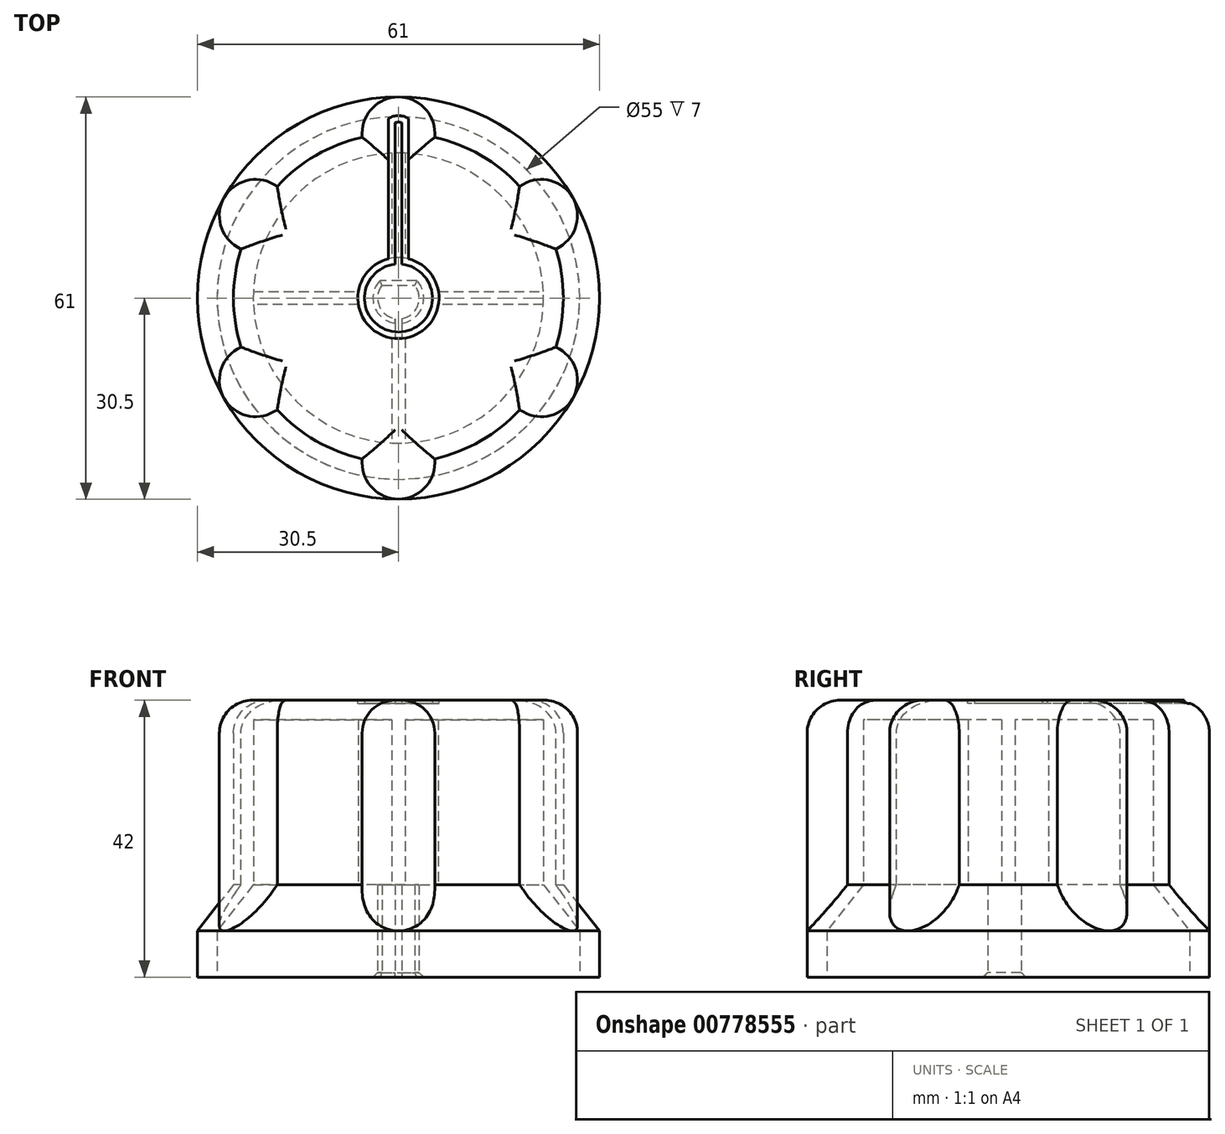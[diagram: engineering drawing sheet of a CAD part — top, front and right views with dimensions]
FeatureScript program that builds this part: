
annotation { "Feature Type Name" : "Feature", "Feature Type Description" : "" }
export const myFeature = defineFeature(function(context is Context, id is Id, definition is map)
    precondition{}
    {
        {
            var Q0;
            Q0=qCreatedBy(makeId("Top.planeOp"),FACE);
            var sketch = newSketch(context, id + "F0", { "sketchPlane" : qUnion([Q0])});
            skCircle(sketch, "E0", {"center": v(0, 0) * mm, "radius": 3.15 * mm});
            skLineSegment(sketch, "E1", {"start": v(-2.47, 1.95) * mm, "end": v(2.47, 1.95) * mm});
            skCircle(sketch, "E2", {"center": v(0, 0) * mm, "radius": 30.5 * mm});
            skCircle(sketch, "E3.0", {"center": v(0, 0) * mm, "radius": 6.15 * mm});
            skLineSegment(sketch, "E4", {"start": v(-0.5, -3.11) * mm, "end": v(-0.5, -6.13) * mm});
            skLineSegment(sketch, "E5", {"start": v(0.5, -3.11) * mm, "end": v(0.5, -6.13) * mm});
            skCircle(sketch, "E6.0", {"center": v(0, 0) * mm, "radius": 27.5 * mm});
            skSolve(sketch);
        }
        {
            var Q0;
            {var subQ0=sQuery(id+"F0.wireOp",EDGE,"E4");Q0=makeQuery(id+"F0.imprint","IMPRINT",FACE,{"disambiguationData":[TD([[makeQuery(id+"F0.imprint","IMPRINT",EDGE,{"derivedFrom":subQ0}),-1.0]])]});}
            var Q1;
            {var subQ0=sQuery(id+"F0.wireOp",EDGE,"E1");Q1=makeQuery(id+"F0.imprint","IMPRINT",FACE,{"disambiguationData":[TD([[makeQuery(id+"F0.imprint","IMPRINT",EDGE,{"derivedFrom":subQ0}),1.0]])]});}
            extrude(context, id + "F1", {"entities" : qUnion([Q0, Q1]), "depth" : 14 * mm, "offsetDistance" : 25 * mm});
        }
        {
            var Q0;
            Q0=makeQuery(id+"F0.imprint","IMPRINT",FACE,{"disambiguationData":[TD([[makeQuery(id+"F0.imprint","IMPRINT",EDGE,{"derivedFrom":sQuery(id+"F0.wireOp",EDGE,"E2")}),1.0]])]});
            extrude(context, id + "F2", {"entities" : qUnion([Q0]), "depth" : 7 * mm, "offsetDistance" : 25 * mm});
        }
        {
            var Q0;
            Q0=makeQuery(id+"F1.opExtrude","CAP_FACE",FACE,{"disambiguationData":[OSD([sQuery(id+"F0.wireOp",EDGE,"E0"),sQuery(id+"F0.wireOp",EDGE,"E1"),sQuery(id+"F0.wireOp",EDGE,"E3.0"),sQuery(id+"F0.wireOp",EDGE,"E4"),sQuery(id+"F0.wireOp",EDGE,"E5")])],"isStart":false});
            var sketch = newSketch(context, id + "F3", { "sketchPlane" : qUnion([Q0])});
            skArc(sketch, "E7.0", {"start": v(0.5, -6.13) * mm, "mid": v(0, 6.15) * mm, "end": v(-0.5, -6.13) * mm});
            skCircle(sketch, "E8", {"center": v(0, 0) * mm, "radius": 25 * mm});
            skCircle(sketch, "E9.0", {"center": v(0, 0) * mm, "radius": 22 * mm});
            skSolve(sketch);
        }
        {
            var Q0;
            Q0=makeQuery(id+"F2.opExtrude","CAP_FACE",FACE,{"disambiguationData":[OSD([sQuery(id+"F0.wireOp",EDGE,"E2"),sQuery(id+"F0.wireOp",EDGE,"E6.0")])],"isStart":false});
            var sketch = newSketch(context, id + "F4", { "sketchPlane" : qUnion([Q0])});
            skCircle(sketch, "E10.0", {"center": v(0, 0) * mm, "radius": 27.5 * mm});
            skCircle(sketch, "E11.0.0", {"center": v(0, 0) * mm, "radius": 30.5 * mm});
            skSolve(sketch);
        }
        {
            var Q0;
            Q0=makeQuery(id+"F3.imprint","IMPRINT",FACE,{"disambiguationData":[TD([[makeQuery(id+"F3.imprint","IMPRINT",EDGE,{"derivedFrom":sQuery(id+"F3.wireOp",EDGE,"E8")}),1.0]])]});
            extrude(context, id + "F5", {"entities" : qUnion([Q0]), "depth" : 25 * mm, "offsetDistance" : 25 * mm});
        }
        {
            var Q0;
            Q0=qCreatedBy(makeId("Right.planeOp"),FACE);
            var sketch = newSketch(context, id + "F6", { "sketchPlane" : qUnion([Q0])});
            skLineSegment(sketch, "E12", {"start": v(-25, 14) * mm, "end": v(-25, 39) * mm});
            skLineSegment(sketch, "E13", {"start": v(-22, 14) * mm, "end": v(-22, 39) * mm});
            skLineSegment(sketch, "E14", {"start": v(22, 39) * mm, "end": v(22, 14) * mm});
            skLineSegment(sketch, "E15", {"start": v(-30.5, 0) * mm, "end": v(-30.5, 7) * mm});
            skLineSegment(sketch, "E16", {"start": v(30.5, 7) * mm, "end": v(30.5, 0) * mm});
            skLineSegment(sketch, "E17.0.0", {"start": v(-27.5, 7) * mm, "end": v(27.5, 7) * mm});
            skLineSegment(sketch, "E18", {"start": v(-22, 14) * mm, "end": v(-27.5, 7) * mm});
            skLineSegment(sketch, "E19", {"start": v(-25, 14) * mm, "end": v(-30.5, 7) * mm});
            skLineSegment(sketch, "E20.0.0", {"start": v(-30.5, 7) * mm, "end": v(30.5, 7) * mm});
            skLineSegment(sketch, "E21.0.0", {"start": v(25, 14) * mm, "end": v(-25, 14) * mm});
            skLineSegment(sketch, "E22.0", {"start": v(-22, 14) * mm, "end": v(22, 14) * mm});
            skSolve(sketch);
        }
        {
            var Q0;
            Q0=qCreatedBy(makeId("Front.planeOp"),FACE);
            var sketch = newSketch(context, id + "F7", { "sketchPlane" : qUnion([Q0])});
            skLineSegment(sketch, "E23", {"start": v(0, 0) * mm, "end": v(0, 40) * mm});
            skSolve(sketch);
        }
        {
            var Q0;
            {var subQ0=sQuery(id+"F6.wireOp",EDGE,"E18");Q0=makeQuery(id+"F6.imprint","IMPRINT",FACE,{"disambiguationData":[TD([[makeQuery(id+"F6.imprint","IMPRINT",EDGE,{"derivedFrom":subQ0}),-1.0]])]});}
            var Q1;
            Q1=sQuery(id+"F7.wireOp",EDGE,"E23");
            revolve(context, id + "F8", {"surfaceOperationType" : NewSurfaceOperationType.NEW, "entities" : qUnion([Q0]), "axis" : qUnion([Q1]), "revolveType" : RevolveType.FULL});
        }
        {
            var Q0;
            Q0=makeQuery(id+"F1.opExtrude","CAP_FACE",FACE,{"disambiguationData":[OSD([sQuery(id+"F0.wireOp",EDGE,"E0"),sQuery(id+"F0.wireOp",EDGE,"E1"),sQuery(id+"F0.wireOp",EDGE,"E3.0"),sQuery(id+"F0.wireOp",EDGE,"E4"),sQuery(id+"F0.wireOp",EDGE,"E5")])],"isStart":false});
            var sketch = newSketch(context, id + "F9", { "sketchPlane" : qUnion([Q0])});
            skCircle(sketch, "E24", {"center": v(0, 0) * mm, "radius": 6.15 * mm});
            skArc(sketch, "E25.0", {"start": v(0.5, -6.13) * mm, "mid": v(0, 6.15) * mm, "end": v(-0.5, -6.13) * mm});
            skCircle(sketch, "E26.0", {"center": v(0, 0) * mm, "radius": 22 * mm});
            skLineSegment(sketch, "E27", {"start": v(-21.98, 1) * mm, "end": v(-6.07, 1) * mm});
            skLineSegment(sketch, "E28", {"start": v(21.98, -1) * mm, "end": v(6.07, -1) * mm});
            skLineSegment(sketch, "E29", {"start": v(-1, 21.98) * mm, "end": v(-1, 6.07) * mm});
            skLineSegment(sketch, "E30", {"start": v(1, 21.98) * mm, "end": v(1, 6.07) * mm});
            skLineSegment(sketch, "E31.trimOffspring", {"start": v(6.07, 1) * mm, "end": v(21.98, 1) * mm});
            skLineSegment(sketch, "E32.trimOffspring", {"start": v(-6.07, -1) * mm, "end": v(-21.98, -1) * mm});
            skLineSegment(sketch, "E33.trimOffspring", {"start": v(1, -6.07) * mm, "end": v(1, -21.98) * mm});
            skLineSegment(sketch, "E34.trimOffspring", {"start": v(-1, -6.07) * mm, "end": v(-1, -21.98) * mm});
            skSolve(sketch);
        }
        {
            var Q0;
            {var subQ0=sQuery(id+"F9.wireOp",EDGE,"E29");Q0=makeQuery(id+"F9.imprint","IMPRINT",FACE,{"disambiguationData":[TD([[makeQuery(id+"F9.imprint","IMPRINT",EDGE,{"derivedFrom":subQ0}),1.0]])]});}
            var Q1;
            {var subQ9=sQuery(id+"F0.wireOp",EDGE,"E1");Q1=makeQuery(id+"F9.imprint","IMPRINT",FACE,{"disambiguationData":[TD([[makeQuery(id+"F9.imprint","IMPRINT",EDGE,{"derivedFrom":makeQuery(id+"F1.opExtrude","CAP_EDGE",EDGE,{"disambiguationData":[OSD([subQ9])],"isStart":false})}),1.0]])]});}
            var Q2;
            {var subQ0=sQuery(id+"F9.wireOp",EDGE,"E28");Q2=makeQuery(id+"F9.imprint","IMPRINT",FACE,{"disambiguationData":[TD([[makeQuery(id+"F9.imprint","IMPRINT",EDGE,{"derivedFrom":subQ0}),-1.0]])]});}
            var Q3;
            {var subQ2=sQuery(id+"F9.wireOp",EDGE,"E33.trimOffspring");Q3=makeQuery(id+"F9.imprint","IMPRINT",FACE,{"disambiguationData":[TD([[makeQuery(id+"F9.imprint","IMPRINT",EDGE,{"derivedFrom":subQ2}),-1.0]])]});}
            var Q4;
            {var subQ0=sQuery(id+"F9.wireOp",EDGE,"E27");Q4=makeQuery(id+"F9.imprint","IMPRINT",FACE,{"disambiguationData":[TD([[makeQuery(id+"F9.imprint","IMPRINT",EDGE,{"derivedFrom":subQ0}),-1.0]])]});}
            var Q5;
            {var subQ0=sQuery(id+"F0.wireOp",EDGE,"E1");Q5=makeQuery(id+"F9.imprint","IMPRINT",FACE,{"disambiguationData":[TD([[makeQuery(id+"F9.imprint","IMPRINT",EDGE,{"derivedFrom":makeQuery(id+"F1.opExtrude","CAP_EDGE",EDGE,{"disambiguationData":[OSD([subQ0])],"isStart":false})}),-1.0]])]});}
            var Q6;
            Q6=makeQuery(id+"F5.opExtrude","CAP_FACE",FACE,{"disambiguationData":[OSD([sQuery(id+"F3.wireOp",EDGE,"E8"),sQuery(id+"F3.wireOp",EDGE,"E9.0")])],"isStart":false});
            extrude(context, id + "F10", {"entities" : qUnion([Q0, Q1, Q2, Q3, Q4, Q5]), "operationType" : NewBodyOperationType.ADD, "endBound" : BoundingType.UP_TO_SURFACE, "depth" : 25 * mm, "endBoundEntityFace" : qUnion([Q6]), "offsetDistance" : 25 * mm});
        }
        {
            var Q0;
            Q0=makeQuery(id+"F5.opExtrude","CAP_FACE",FACE,{"disambiguationData":[OSD([sQuery(id+"F3.wireOp",EDGE,"E8"),sQuery(id+"F3.wireOp",EDGE,"E9.0")])],"isStart":false});
            var sketch = newSketch(context, id + "F11", { "sketchPlane" : qUnion([Q0])});
            skCircle(sketch, "E35.0", {"center": v(0, 0) * mm, "radius": 25 * mm});
            skSolve(sketch);
        }
        {
            var Q0;
            Q0 = qSketchRegion(id + "F11", true);
            extrude(context, id + "F12", {"entities" : qUnion([Q0]), "depth" : 3 * mm, "offsetDistance" : 25 * mm});
        }
        {
            var Q0;
            Q0=makeQuery(id+"F12.opExtrude","CAP_FACE",FACE,{"disambiguationData":[OSD([sQuery(id+"F11.wireOp",EDGE,"E35.0")])],"isStart":false});
            var sketch = newSketch(context, id + "F13", { "sketchPlane" : qUnion([Q0])});
            skCircle(sketch, "E36.0", {"center": v(0, 0) * mm, "radius": 25 * mm});
            skCircle(sketch, "E37.0", {"center": v(0, 0) * mm, "radius": 30.5 * mm});
            skArc(sketch, "E38", {"start": v(5.5, 25) * mm, "mid": v(0, 30.5) * mm, "end": v(-5.5, 25) * mm});
            skLineSegment(sketch, "E39", {"start": v(-5.5, 25) * mm, "end": v(-5.5, 24.39) * mm});
            skLineSegment(sketch, "E40", {"start": v(5.5, 25) * mm, "end": v(5.5, 24.39) * mm});
            skArc(sketch, "E41.1.0", {"start": v(-18.9, 17.26) * mm, "mid": v(-26.41, 15.25) * mm, "end": v(-24.4, 7.74) * mm});
            skLineSegment(sketch, "E41.1.1", {"start": v(-24.4, 7.74) * mm, "end": v(-23.87, 7.43) * mm});
            skLineSegment(sketch, "E41.1.2", {"start": v(-18.9, 17.26) * mm, "end": v(-18.37, 16.96) * mm});
            skArc(sketch, "E41.2.0", {"start": v(-24.4, -7.74) * mm, "mid": v(-26.41, -15.25) * mm, "end": v(-18.9, -17.26) * mm});
            skLineSegment(sketch, "E41.2.1", {"start": v(-18.9, -17.26) * mm, "end": v(-18.37, -16.96) * mm});
            skLineSegment(sketch, "E41.2.2", {"start": v(-24.4, -7.74) * mm, "end": v(-23.87, -7.43) * mm});
            skArc(sketch, "E41.3.0", {"start": v(-5.5, -25) * mm, "mid": v(0, -30.5) * mm, "end": v(5.5, -25) * mm});
            skLineSegment(sketch, "E41.3.1", {"start": v(5.5, -25) * mm, "end": v(5.5, -24.39) * mm});
            skLineSegment(sketch, "E41.3.2", {"start": v(-5.5, -25) * mm, "end": v(-5.5, -24.39) * mm});
            skArc(sketch, "E41.4.0", {"start": v(18.9, -17.26) * mm, "mid": v(26.41, -15.25) * mm, "end": v(24.4, -7.74) * mm});
            skLineSegment(sketch, "E41.4.1", {"start": v(24.4, -7.74) * mm, "end": v(23.87, -7.43) * mm});
            skLineSegment(sketch, "E41.4.2", {"start": v(18.9, -17.26) * mm, "end": v(18.37, -16.96) * mm});
            skArc(sketch, "E41.5.0", {"start": v(24.4, 7.74) * mm, "mid": v(26.41, 15.25) * mm, "end": v(18.9, 17.26) * mm});
            skLineSegment(sketch, "E41.5.1", {"start": v(18.9, 17.26) * mm, "end": v(18.37, 16.96) * mm});
            skLineSegment(sketch, "E41.5.2", {"start": v(24.4, 7.74) * mm, "end": v(23.87, 7.43) * mm});
            skSolve(sketch);
        }
        {
            var Q0;
            {var subQ0=sQuery(id+"F13.wireOp",EDGE,"E39");Q0=makeQuery(id+"F13.imprint","IMPRINT",FACE,{"disambiguationData":[TD([[makeQuery(id+"F13.imprint","IMPRINT",EDGE,{"derivedFrom":subQ0}),1.0]])]});}
            var Q1;
            {var subQ0=sQuery(id+"F13.wireOp",EDGE,"E41.1.1");Q1=makeQuery(id+"F13.imprint","IMPRINT",FACE,{"disambiguationData":[TD([[makeQuery(id+"F13.imprint","IMPRINT",EDGE,{"derivedFrom":subQ0}),1.0]])]});}
            var Q2;
            {var subQ0=sQuery(id+"F13.wireOp",EDGE,"E41.5.1");Q2=makeQuery(id+"F13.imprint","IMPRINT",FACE,{"disambiguationData":[TD([[makeQuery(id+"F13.imprint","IMPRINT",EDGE,{"derivedFrom":subQ0}),1.0]])]});}
            var Q3;
            {var subQ0=sQuery(id+"F13.wireOp",EDGE,"E41.4.1");Q3=makeQuery(id+"F13.imprint","IMPRINT",FACE,{"disambiguationData":[TD([[makeQuery(id+"F13.imprint","IMPRINT",EDGE,{"derivedFrom":subQ0}),1.0]])]});}
            var Q4;
            {var subQ0=sQuery(id+"F13.wireOp",EDGE,"E41.2.1");Q4=makeQuery(id+"F13.imprint","IMPRINT",FACE,{"disambiguationData":[TD([[makeQuery(id+"F13.imprint","IMPRINT",EDGE,{"derivedFrom":subQ0}),1.0]])]});}
            var Q5;
            {var subQ0=sQuery(id+"F13.wireOp",EDGE,"E41.3.1");Q5=makeQuery(id+"F13.imprint","IMPRINT",FACE,{"disambiguationData":[TD([[makeQuery(id+"F13.imprint","IMPRINT",EDGE,{"derivedFrom":subQ0}),1.0]])]});}
            var Q6;
            Q6=makeQuery(id+"F8.opRevolve","SWEPT_FACE",FACE,{"disambiguationData":[OSD([sQuery(id+"F6.wireOp",EDGE,"E19")])]});
            var Q7;
            Q7=makeQuery(id+"F8.opRevolve","SWEPT_BODY",BODY,{"disambiguationData":[OSD([sQuery(id+"F6.wireOp",EDGE,"E18"),sQuery(id+"F6.wireOp",EDGE,"E19"),sQuery(id+"F6.wireOp",EDGE,"E20.0.0"),sQuery(id+"F6.wireOp",EDGE,"E21.0.0")])]});
            extrude(context, id + "F14", {"entities" : qUnion([Q0, Q1, Q2, Q3, Q4, Q5]), "operationType" : NewBodyOperationType.ADD, "endBound" : BoundingType.UP_TO_NEXT, "oppositeDirection" : true, "depth" : 25 * mm, "endBoundEntityFace" : qUnion([Q6]), "endBoundEntityBody" : qUnion([Q7]), "offsetDistance" : 25 * mm});
        }
        {
            var Q0;
            {var subQ0=sQuery(id+"F13.wireOp",EDGE,"E36.0");Q0=makeQuery(id+"F14.boolean.opBoolean","MERGE",FACE,{"derivedFrom":[makeQuery(id+"F12.opExtrude","CAP_FACE",FACE,{"disambiguationData":[OSD([sQuery(id+"F11.wireOp",EDGE,"E35.0")])],"isStart":false}),makeQuery(id+"F14.opExtrude","CAP_FACE",FACE,{"disambiguationData":[OSD([subQ0,sQuery(id+"F13.wireOp",EDGE,"E41.5.0"),sQuery(id+"F13.wireOp",EDGE,"E41.5.1"),sQuery(id+"F13.wireOp",EDGE,"E41.5.2")])],"isStart":true}),makeQuery(id+"F14.opExtrude","CAP_FACE",FACE,{"disambiguationData":[OSD([subQ0,sQuery(id+"F13.wireOp",EDGE,"E38"),sQuery(id+"F13.wireOp",EDGE,"E39"),sQuery(id+"F13.wireOp",EDGE,"E40")])],"isStart":true}),makeQuery(id+"F14.opExtrude","CAP_FACE",FACE,{"disambiguationData":[OSD([subQ0,sQuery(id+"F13.wireOp",EDGE,"E41.1.0"),sQuery(id+"F13.wireOp",EDGE,"E41.1.1"),sQuery(id+"F13.wireOp",EDGE,"E41.1.2")])],"isStart":true}),makeQuery(id+"F14.opExtrude","CAP_FACE",FACE,{"disambiguationData":[OSD([subQ0,sQuery(id+"F13.wireOp",EDGE,"E41.2.0"),sQuery(id+"F13.wireOp",EDGE,"E41.2.1"),sQuery(id+"F13.wireOp",EDGE,"E41.2.2")])],"isStart":true}),makeQuery(id+"F14.opExtrude","CAP_FACE",FACE,{"disambiguationData":[OSD([subQ0,sQuery(id+"F13.wireOp",EDGE,"E41.3.0"),sQuery(id+"F13.wireOp",EDGE,"E41.3.1"),sQuery(id+"F13.wireOp",EDGE,"E41.3.2")])],"isStart":true}),makeQuery(id+"F14.opExtrude","CAP_FACE",FACE,{"disambiguationData":[OSD([subQ0,sQuery(id+"F13.wireOp",EDGE,"E41.4.0"),sQuery(id+"F13.wireOp",EDGE,"E41.4.1"),sQuery(id+"F13.wireOp",EDGE,"E41.4.2")])],"isStart":true})]});}
            var sketch = newSketch(context, id + "F15", { "sketchPlane" : qUnion([Q0])});
            skCircle(sketch, "E42.0", {"center": v(0, 0) * mm, "radius": 6.15 * mm});
            skArc(sketch, "E43.0", {"start": v(5.5, 25) * mm, "mid": v(0, 30.5) * mm, "end": v(-5.5, 25) * mm});
            skLineSegment(sketch, "E44", {"start": v(-1.5, 30.3) * mm, "end": v(-1.5, 5.96) * mm});
            skLineSegment(sketch, "E45", {"start": v(1.5, 30.3) * mm, "end": v(1.5, 5.96) * mm});
            skSolve(sketch);
        }
        {
            var Q0;
            {var subQ2=sQuery(id+"F13.wireOp",EDGE,"E40");var subQ3=sQuery(id+"F11.wireOp",EDGE,"E35.0");Q0=makeQuery(id+"F14.boolean.opBoolean","SPLIT",EDGE,{"disambiguationData":[TD([makeQuery(id+"F14.opExtrude","SWEPT_FACE",FACE,{"disambiguationData":[OSD([subQ2])]})])],"derivedFrom":makeQuery(id+"F12.opExtrude","CAP_EDGE",EDGE,{"disambiguationData":[OSD([subQ3])],"isStart":false})});}
            var Q1;
            Q1=makeQuery(id+"F14.opExtrude","CAP_EDGE",EDGE,{"disambiguationData":[OSD([sQuery(id+"F13.wireOp",EDGE,"E41.5.0")])],"isStart":true});
            var Q2;
            {var subQ0=sQuery(id+"F13.wireOp",EDGE,"E41.4.1");var subQ2=sQuery(id+"F11.wireOp",EDGE,"E35.0");Q2=makeQuery(id+"F14.boolean.opBoolean","SPLIT",EDGE,{"disambiguationData":[TD([makeQuery(id+"F14.opExtrude","SWEPT_FACE",FACE,{"disambiguationData":[OSD([subQ0])]})])],"derivedFrom":makeQuery(id+"F12.opExtrude","CAP_EDGE",EDGE,{"disambiguationData":[OSD([subQ2])],"isStart":false})});}
            var Q3;
            Q3=makeQuery(id+"F14.opExtrude","CAP_EDGE",EDGE,{"disambiguationData":[OSD([sQuery(id+"F13.wireOp",EDGE,"E41.4.0")])],"isStart":true});
            var Q4;
            {var subQ0=sQuery(id+"F13.wireOp",EDGE,"E41.3.1");var subQ3=sQuery(id+"F11.wireOp",EDGE,"E35.0");Q4=makeQuery(id+"F14.boolean.opBoolean","SPLIT",EDGE,{"disambiguationData":[TD([makeQuery(id+"F14.opExtrude","SWEPT_FACE",FACE,{"disambiguationData":[OSD([subQ0])]})])],"derivedFrom":makeQuery(id+"F12.opExtrude","CAP_EDGE",EDGE,{"disambiguationData":[OSD([subQ3])],"isStart":false})});}
            var Q5;
            Q5=makeQuery(id+"F14.opExtrude","CAP_EDGE",EDGE,{"disambiguationData":[OSD([sQuery(id+"F13.wireOp",EDGE,"E41.3.0")])],"isStart":true});
            var Q6;
            {var subQ0=sQuery(id+"F13.wireOp",EDGE,"E41.2.1");var subQ1=sQuery(id+"F11.wireOp",EDGE,"E35.0");Q6=makeQuery(id+"F14.boolean.opBoolean","SPLIT",EDGE,{"disambiguationData":[TD([makeQuery(id+"F14.opExtrude","SWEPT_FACE",FACE,{"disambiguationData":[OSD([subQ0])]})])],"derivedFrom":makeQuery(id+"F12.opExtrude","CAP_EDGE",EDGE,{"disambiguationData":[OSD([subQ1])],"isStart":false})});}
            var Q7;
            Q7=makeQuery(id+"F14.opExtrude","CAP_EDGE",EDGE,{"disambiguationData":[OSD([sQuery(id+"F13.wireOp",EDGE,"E41.2.0")])],"isStart":true});
            var Q8;
            {var subQ2=sQuery(id+"F13.wireOp",EDGE,"E41.1.1");var subQ3=sQuery(id+"F11.wireOp",EDGE,"E35.0");Q8=makeQuery(id+"F14.boolean.opBoolean","SPLIT",EDGE,{"disambiguationData":[TD([makeQuery(id+"F14.opExtrude","SWEPT_FACE",FACE,{"disambiguationData":[OSD([subQ2])]})])],"derivedFrom":makeQuery(id+"F12.opExtrude","CAP_EDGE",EDGE,{"disambiguationData":[OSD([subQ3])],"isStart":false})});}
            var Q9;
            Q9=makeQuery(id+"F14.opExtrude","CAP_EDGE",EDGE,{"disambiguationData":[OSD([sQuery(id+"F13.wireOp",EDGE,"E41.1.0")])],"isStart":true});
            var Q10;
            {var subQ0=sQuery(id+"F13.wireOp",EDGE,"E39");var subQ3=sQuery(id+"F11.wireOp",EDGE,"E35.0");Q10=makeQuery(id+"F14.boolean.opBoolean","SPLIT",EDGE,{"disambiguationData":[TD([makeQuery(id+"F14.opExtrude","SWEPT_FACE",FACE,{"disambiguationData":[OSD([subQ0])]})])],"derivedFrom":makeQuery(id+"F12.opExtrude","CAP_EDGE",EDGE,{"disambiguationData":[OSD([subQ3])],"isStart":false})});}
            var Q11;
            Q11=makeQuery(id+"F14.opExtrude","CAP_EDGE",EDGE,{"disambiguationData":[OSD([sQuery(id+"F13.wireOp",EDGE,"E38")])],"isStart":true});
            var Q12;
            Q12=makeQuery(id+"F14.opExtrude","CAP_EDGE",EDGE,{"disambiguationData":[OSD([sQuery(id+"F13.wireOp",EDGE,"E41.5.2")])],"isStart":true});
            var Q13;
            Q13=makeQuery(id+"F14.opExtrude","CAP_EDGE",EDGE,{"disambiguationData":[OSD([sQuery(id+"F13.wireOp",EDGE,"E41.4.1")])],"isStart":true});
            var Q14;
            Q14=makeQuery(id+"F14.opExtrude","CAP_EDGE",EDGE,{"disambiguationData":[OSD([sQuery(id+"F13.wireOp",EDGE,"E41.4.2")])],"isStart":true});
            var Q15;
            Q15=makeQuery(id+"F14.opExtrude","CAP_EDGE",EDGE,{"disambiguationData":[OSD([sQuery(id+"F13.wireOp",EDGE,"E41.3.1")])],"isStart":true});
            var Q16;
            Q16=makeQuery(id+"F14.opExtrude","CAP_EDGE",EDGE,{"disambiguationData":[OSD([sQuery(id+"F13.wireOp",EDGE,"E41.3.2")])],"isStart":true});
            var Q17;
            Q17=makeQuery(id+"F14.opExtrude","CAP_EDGE",EDGE,{"disambiguationData":[OSD([sQuery(id+"F13.wireOp",EDGE,"E41.2.1")])],"isStart":true});
            var Q18;
            Q18=makeQuery(id+"F14.opExtrude","CAP_EDGE",EDGE,{"disambiguationData":[OSD([sQuery(id+"F13.wireOp",EDGE,"E41.2.2")])],"isStart":true});
            var Q19;
            Q19=makeQuery(id+"F14.opExtrude","CAP_EDGE",EDGE,{"disambiguationData":[OSD([sQuery(id+"F13.wireOp",EDGE,"E41.1.1")])],"isStart":true});
            var Q20;
            Q20=makeQuery(id+"F14.opExtrude","CAP_EDGE",EDGE,{"disambiguationData":[OSD([sQuery(id+"F13.wireOp",EDGE,"E41.1.2")])],"isStart":true});
            var Q21;
            Q21=makeQuery(id+"F14.opExtrude","CAP_EDGE",EDGE,{"disambiguationData":[OSD([sQuery(id+"F13.wireOp",EDGE,"E39")])],"isStart":true});
            var Q22;
            Q22=makeQuery(id+"F14.opExtrude","CAP_EDGE",EDGE,{"disambiguationData":[OSD([sQuery(id+"F13.wireOp",EDGE,"E40")])],"isStart":true});
            var Q23;
            Q23=makeQuery(id+"F14.opExtrude","CAP_EDGE",EDGE,{"disambiguationData":[OSD([sQuery(id+"F13.wireOp",EDGE,"E41.5.1")])],"isStart":true});
            fillet(context, id + "F16", {"entities" : qUnion([Q0, Q1, Q2, Q3, Q4, Q5, Q6, Q7, Q8, Q9, Q10, Q11, Q12, Q13, Q14, Q15, Q16, Q17, Q18, Q19, Q20, Q21, Q22, Q23]), "radius" : 5 * mm, "tangentPropagation" : true, "allowEdgeOverflow" : false});
        }
        {
            var Q0;
            {var subQ0=sQuery(id+"F15.wireOp",EDGE,"E42.0");var subQ1=makeQuery(id+"F15.imprint","INTERSECT",VERTEX,{"derivedFrom":[subQ0,sQuery(id+"F15.wireOp",EDGE,"E44")]});Q0=makeQuery(id+"F15.imprint","IMPRINT",FACE,{"disambiguationData":[TD([[makeQuery(id+"F15.imprint","IMPRINT",EDGE,{"disambiguationData":[TD([[subQ1,1.0]])],"derivedFrom":subQ0}),1.0]])]});}
            var Q1;
            {var subQ0=sQuery(id+"F15.wireOp",EDGE,"E44");Q1=makeQuery(id+"F15.imprint","IMPRINT",FACE,{"disambiguationData":[TD([[makeQuery(id+"F15.imprint","IMPRINT",EDGE,{"derivedFrom":subQ0}),1.0]])]});}
            extrude(context, id + "F17", {"entities" : qUnion([Q0, Q1]), "operationType" : NewBodyOperationType.REMOVE, "oppositeDirection" : true, "depth" : .5 * mm, "offsetDistance" : 25 * mm});
        }
        {
            var Q0;
            Q0=makeQuery(id+"F17.boolean.opBoolean","COPY",FACE,{"derivedFrom":makeQuery(id+"F17.opExtrude","CAP_FACE",FACE,{"disambiguationData":[OSD([sQuery(id+"F15.wireOp",EDGE,"E42.0"),sQuery(id+"F15.wireOp",EDGE,"E43.0"),sQuery(id+"F15.wireOp",EDGE,"E44"),sQuery(id+"F15.wireOp",EDGE,"E45")])],"isStart":false})});
            var sketch = newSketch(context, id + "F18", { "sketchPlane" : qUnion([Q0])});
            skLineSegment(sketch, "E46.0.0", {"start": v(-1.5, 27.22) * mm, "end": v(-1.5, 5.96) * mm});
            skArc(sketch, "E46.0.1", {"start": v(-1.5, 5.96) * mm, "mid": v(0, -6.15) * mm, "end": v(1.5, 5.96) * mm});
            skLineSegment(sketch, "E46.0.2", {"start": v(1.5, 5.96) * mm, "end": v(1.5, 27.22) * mm});
            skArc(sketch, "E46.0.3", {"start": v(-1.5, 27.22) * mm, "mid": v(0, 27.68) * mm, "end": v(1.5, 27.22) * mm});
            skLineSegment(sketch, "E47.0", {"start": v(-0.5, 26.6) * mm, "end": v(-0.5, 5.13) * mm});
            skArc(sketch, "E47.1", {"start": v(-0.5, 26.6) * mm, "mid": v(0, 26.68) * mm, "end": v(0.5, 26.6) * mm});
            skLineSegment(sketch, "E47.2", {"start": v(0.5, 5.13) * mm, "end": v(0.5, 26.6) * mm});
            skArc(sketch, "E47.3", {"start": v(-0.5, 5.13) * mm, "mid": v(0, -5.15) * mm, "end": v(0.5, 5.13) * mm});
            skSolve(sketch);
        }
        {
            var Q0;
            Q0=makeQuery(id+"F18.imprint","IMPRINT",FACE,{"disambiguationData":[TD([[makeQuery(id+"F18.imprint","IMPRINT",EDGE,{"derivedFrom":sQuery(id+"F18.wireOp",EDGE,"E47.0")}),1.0]])]});
            var Q1;
            {var subQ0=sQuery(id+"F13.wireOp",EDGE,"E36.0");Q1=makeQuery(id+"F14.boolean.opBoolean","MERGE",FACE,{"derivedFrom":[makeQuery(id+"F12.opExtrude","CAP_FACE",FACE,{"disambiguationData":[OSD([sQuery(id+"F11.wireOp",EDGE,"E35.0")])],"isStart":false}),makeQuery(id+"F14.opExtrude","CAP_FACE",FACE,{"disambiguationData":[OSD([subQ0,sQuery(id+"F13.wireOp",EDGE,"E41.5.0"),sQuery(id+"F13.wireOp",EDGE,"E41.5.1"),sQuery(id+"F13.wireOp",EDGE,"E41.5.2")])],"isStart":true}),makeQuery(id+"F14.opExtrude","CAP_FACE",FACE,{"disambiguationData":[OSD([subQ0,sQuery(id+"F13.wireOp",EDGE,"E38"),sQuery(id+"F13.wireOp",EDGE,"E39"),sQuery(id+"F13.wireOp",EDGE,"E40")])],"isStart":true}),makeQuery(id+"F14.opExtrude","CAP_FACE",FACE,{"disambiguationData":[OSD([subQ0,sQuery(id+"F13.wireOp",EDGE,"E41.1.0"),sQuery(id+"F13.wireOp",EDGE,"E41.1.1"),sQuery(id+"F13.wireOp",EDGE,"E41.1.2")])],"isStart":true}),makeQuery(id+"F14.opExtrude","CAP_FACE",FACE,{"disambiguationData":[OSD([subQ0,sQuery(id+"F13.wireOp",EDGE,"E41.2.0"),sQuery(id+"F13.wireOp",EDGE,"E41.2.1"),sQuery(id+"F13.wireOp",EDGE,"E41.2.2")])],"isStart":true}),makeQuery(id+"F14.opExtrude","CAP_FACE",FACE,{"disambiguationData":[OSD([subQ0,sQuery(id+"F13.wireOp",EDGE,"E41.3.0"),sQuery(id+"F13.wireOp",EDGE,"E41.3.1"),sQuery(id+"F13.wireOp",EDGE,"E41.3.2")])],"isStart":true}),makeQuery(id+"F14.opExtrude","CAP_FACE",FACE,{"disambiguationData":[OSD([subQ0,sQuery(id+"F13.wireOp",EDGE,"E41.4.0"),sQuery(id+"F13.wireOp",EDGE,"E41.4.1"),sQuery(id+"F13.wireOp",EDGE,"E41.4.2")])],"isStart":true})]});}
            extrude(context, id + "F19", {"entities" : qUnion([Q0]), "operationType" : NewBodyOperationType.ADD, "endBound" : BoundingType.UP_TO_SURFACE, "depth" : 25 * mm, "endBoundEntityFace" : qUnion([Q1]), "offsetDistance" : 25 * mm});
        }
        {
            var Q0;
            {var subQ0=sQuery(id+"F0.wireOp",EDGE,"E0");Q0=makeQuery(id+"F1.opExtrude","CAP_EDGE",EDGE,{"disambiguationData":[OSD([subQ0]),TDD([makeQuery(id+"F0.imprint","IMPRINT",EDGE,{"disambiguationData":[TD([[makeQuery(id+"F0.imprint","INTERSECT",VERTEX,{"disambiguationData":[OD(0.0)],"derivedFrom":[subQ0,sQuery(id+"F0.wireOp",EDGE,"E1")]}),-1.0]])],"derivedFrom":subQ0})])],"isStart":true});}
            var Q1;
            Q1=makeQuery(id+"F1.opExtrude","CAP_EDGE",EDGE,{"disambiguationData":[OSD([sQuery(id+"F0.wireOp",EDGE,"E1")])],"isStart":true});
            var Q2;
            {var subQ0=sQuery(id+"F0.wireOp",EDGE,"E0");Q2=makeQuery(id+"F1.opExtrude","CAP_EDGE",EDGE,{"disambiguationData":[OSD([subQ0]),TDD([makeQuery(id+"F0.imprint","IMPRINT",EDGE,{"disambiguationData":[TD([[makeQuery(id+"F0.imprint","INTERSECT",VERTEX,{"disambiguationData":[OD(1.0)],"derivedFrom":[subQ0,sQuery(id+"F0.wireOp",EDGE,"E1")]}),1.0]])],"derivedFrom":subQ0})])],"isStart":true});}
            chamfer(context, id + "F20", {"entities" : qUnion([Q0, Q1, Q2]), "width" : .7 * mm, "tangentPropagation" : true});
        }
    });
